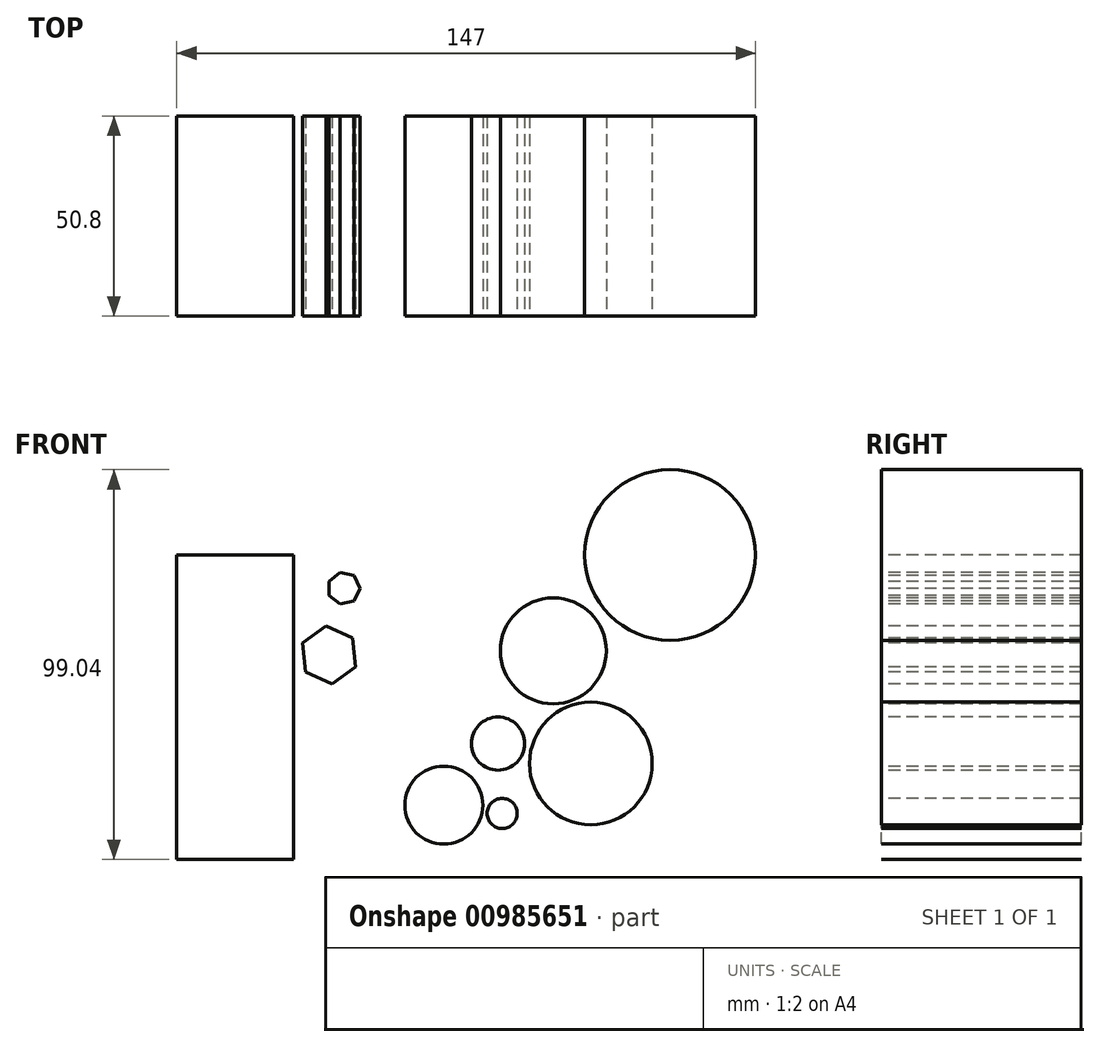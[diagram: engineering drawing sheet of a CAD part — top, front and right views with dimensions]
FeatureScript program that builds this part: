
annotation { "Feature Type Name" : "Feature", "Feature Type Description" : "" }
export const myFeature = defineFeature(function(context is Context, id is Id, definition is map)
    precondition{}
    {
        {
            var Q0;
            Q0=qCreatedBy(makeId("Front.planeOp"),FACE);
            var sketch = newSketch(context, id + "F0", { "sketchPlane" : qUnion([Q0])});
            skLineSegment(sketch, "E0.bottom", {"start": v(-60.54, 36.7) * mm, "end": v(64.78, 36.7) * mm});
            skLineSegment(sketch, "E0.top", {"start": v(-60.54, -40.67) * mm, "end": v(64.78, -40.67) * mm});
            skLineSegment(sketch, "E0.left", {"start": v(-60.54, 36.7) * mm, "end": v(-60.54, -40.67) * mm});
            skLineSegment(sketch, "E0.right", {"start": v(64.78, 36.7) * mm, "end": v(64.78, -40.67) * mm});
            skLineSegment(sketch, "E1.bottom", {"start": v(-60.54, 36.7) * mm, "end": v(-30.86, 36.7) * mm});
            skLineSegment(sketch, "E1.top", {"start": v(-60.54, 8.88) * mm, "end": v(-30.86, 8.88) * mm});
            skLineSegment(sketch, "E1.left", {"start": v(-60.54, 36.7) * mm, "end": v(-60.54, 8.88) * mm});
            skLineSegment(sketch, "E1.right", {"start": v(-30.86, 36.7) * mm, "end": v(-30.86, 8.88) * mm});
            skLineSegment(sketch, "E2.bottom", {"start": v(-45.7, 8.88) * mm, "end": v(-30.86, 8.88) * mm});
            skLineSegment(sketch, "E2.top", {"start": v(-45.7, 0) * mm, "end": v(-30.86, 0) * mm});
            skLineSegment(sketch, "E2.left", {"start": v(-45.7, 8.88) * mm, "end": v(-45.7, 0) * mm});
            skLineSegment(sketch, "E2.right", {"start": v(-30.86, 8.88) * mm, "end": v(-30.86, 0) * mm});
            skLineSegment(sketch, "E3.bottom", {"start": v(-38.28, 0) * mm, "end": v(-30.86, 0) * mm});
            skLineSegment(sketch, "E3.top", {"start": v(-38.28, -7.29) * mm, "end": v(-30.86, -7.29) * mm});
            skLineSegment(sketch, "E3.left", {"start": v(-38.28, 0) * mm, "end": v(-38.28, -7.29) * mm});
            skLineSegment(sketch, "E3.right", {"start": v(-30.86, 0) * mm, "end": v(-30.86, -7.29) * mm});
            skLineSegment(sketch, "E4.bottom", {"start": v(-34.57, -7.29) * mm, "end": v(-30.86, -7.29) * mm});
            skLineSegment(sketch, "E4.top", {"start": v(-34.57, -40.67) * mm, "end": v(-30.86, -40.67) * mm});
            skLineSegment(sketch, "E4.left", {"start": v(-34.57, -7.29) * mm, "end": v(-34.57, -40.67) * mm});
            skLineSegment(sketch, "E4.right", {"start": v(-30.86, -7.29) * mm, "end": v(-30.86, -40.67) * mm});
            skCircle(sketch, "E5", {"center": v(64.78, 36.7) * mm, "radius": 21.68 * mm});
            skCircle(sketch, "E6", {"center": v(35.1, 12.32) * mm, "radius": 13.46 * mm});
            skCircle(sketch, "E7", {"center": v(44.64, -16.3) * mm, "radius": 15.59 * mm});
            skCircle(sketch, "E8", {"center": v(7.29, -26.9) * mm, "radius": 9.9 * mm});
            skCircle(sketch, "E9", {"center": v(22.12, -29.01) * mm, "radius": 3.82 * mm});
            skCircle(sketch, "E10", {"center": v(21.06, -11.26) * mm, "radius": 6.75 * mm});
            skCircle(sketch, "E11.cCircle", {"center": v(-18.15, 28.22) * mm, "radius": 3.7 * mm, "construction": true});
            skLineSegment(sketch, "E11.0", {"start": v(-21.86, 26.43) * mm, "end": v(-21.86, 30) * mm});
            skLineSegment(sketch, "E11.1", {"start": v(-21.86, 30) * mm, "end": v(-19.06, 32.23) * mm});
            skLineSegment(sketch, "E11.2", {"start": v(-19.06, 32.23) * mm, "end": v(-15.58, 31.43) * mm});
            skLineSegment(sketch, "E11.3", {"start": v(-15.58, 31.43) * mm, "end": v(-14.03, 28.22) * mm});
            skLineSegment(sketch, "E11.4", {"start": v(-14.03, 28.22) * mm, "end": v(-15.58, 25) * mm});
            skLineSegment(sketch, "E11.5", {"start": v(-15.58, 25) * mm, "end": v(-19.06, 24.2) * mm});
            skLineSegment(sketch, "E11.6", {"start": v(-19.06, 24.2) * mm, "end": v(-21.86, 26.43) * mm});
            skPoint(sketch, "E11.0.midPoint", {"position": v(-21.86, 28.22) * mm});
            skCircle(sketch, "E12.cCircle", {"center": v(-21.86, 11.26) * mm, "radius": 6.4 * mm, "construction": true});
            skLineSegment(sketch, "E12.0", {"start": v(-21.14, 3.9) * mm, "end": v(-27.87, 6.96) * mm});
            skLineSegment(sketch, "E12.1", {"start": v(-27.87, 6.96) * mm, "end": v(-28.59, 14.32) * mm});
            skLineSegment(sketch, "E12.2", {"start": v(-28.59, 14.32) * mm, "end": v(-22.57, 18.62) * mm});
            skLineSegment(sketch, "E12.3", {"start": v(-22.57, 18.62) * mm, "end": v(-15.84, 15.56) * mm});
            skLineSegment(sketch, "E12.4", {"start": v(-15.84, 15.56) * mm, "end": v(-15.13, 8.2) * mm});
            skLineSegment(sketch, "E12.5", {"start": v(-15.13, 8.2) * mm, "end": v(-21.14, 3.9) * mm});
            skPoint(sketch, "E12.0.midPoint", {"position": v(-24.5, 5.43) * mm});
            skSolve(sketch);
        }
        {
            var Q0;
            {var subQ6=sQuery(id+"F0.wireOp",EDGE,"E1.right");Q0=makeQuery(id+"F0.imprint","IMPRINT",FACE,{"disambiguationData":[TD([[makeQuery(id+"F0.imprint","IMPRINT",EDGE,{"derivedFrom":subQ6}),-1.0]])]});}
            var Q1;
            Q1=makeQuery(id+"F0.imprint","IMPRINT",FACE,{"disambiguationData":[TD([[makeQuery(id+"F0.imprint","IMPRINT",EDGE,{"derivedFrom":sQuery(id+"F0.wireOp",EDGE,"E8")}),1.0]])]});
            var Q2;
            Q2=makeQuery(id+"F0.imprint","IMPRINT",FACE,{"disambiguationData":[TD([[makeQuery(id+"F0.imprint","IMPRINT",EDGE,{"derivedFrom":sQuery(id+"F0.wireOp",EDGE,"E12.0")}),-1.0]])]});
            var Q3;
            Q3=makeQuery(id+"F0.imprint","IMPRINT",FACE,{"disambiguationData":[TD([[makeQuery(id+"F0.imprint","IMPRINT",EDGE,{"derivedFrom":sQuery(id+"F0.wireOp",EDGE,"E11.0")}),-1.0]])]});
            var Q4;
            Q4=makeQuery(id+"F0.imprint","IMPRINT",FACE,{"disambiguationData":[TD([[makeQuery(id+"F0.imprint","IMPRINT",EDGE,{"derivedFrom":sQuery(id+"F0.wireOp",EDGE,"E6")}),1.0]])]});
            var Q5;
            {var subQ0=sQuery(id+"F0.wireOp",EDGE,"E0.right");var subQ1=sQuery(id+"F0.wireOp",EDGE,"E0.bottom");var subQ2=makeQuery(id+"F0.imprint","INTERSECT",VERTEX,{"derivedFrom":[subQ1,subQ0]});Q5=makeQuery(id+"F0.imprint","IMPRINT",FACE,{"disambiguationData":[TD([[makeQuery(id+"F0.imprint","IMPRINT",EDGE,{"disambiguationData":[TD([[subQ2,1.0]])],"derivedFrom":subQ1}),-1.0]])]});}
            var Q6;
            {var subQ0=sQuery(id+"F0.wireOp",EDGE,"E0.right");var subQ1=sQuery(id+"F0.wireOp",EDGE,"E0.bottom");var subQ2=makeQuery(id+"F0.imprint","INTERSECT",VERTEX,{"derivedFrom":[subQ1,subQ0]});Q6=makeQuery(id+"F0.imprint","IMPRINT",FACE,{"disambiguationData":[TD([[makeQuery(id+"F0.imprint","IMPRINT",EDGE,{"disambiguationData":[TD([[subQ2,1.0]])],"derivedFrom":subQ1}),1.0]])]});}
            var Q7;
            Q7=makeQuery(id+"F0.imprint","IMPRINT",FACE,{"disambiguationData":[TD([[makeQuery(id+"F0.imprint","IMPRINT",EDGE,{"derivedFrom":sQuery(id+"F0.wireOp",EDGE,"E7")}),1.0]])]});
            var Q8;
            Q8=makeQuery(id+"F0.imprint","IMPRINT",FACE,{"disambiguationData":[TD([[makeQuery(id+"F0.imprint","IMPRINT",EDGE,{"derivedFrom":sQuery(id+"F0.wireOp",EDGE,"E10")}),1.0]])]});
            var Q9;
            Q9=makeQuery(id+"F0.imprint","IMPRINT",FACE,{"disambiguationData":[TD([[makeQuery(id+"F0.imprint","IMPRINT",EDGE,{"derivedFrom":sQuery(id+"F0.wireOp",EDGE,"E9")}),1.0]])]});
            var Q10;
            {var subQ2=sQuery(id+"F0.wireOp",EDGE,"E4.left");Q10=makeQuery(id+"F0.imprint","IMPRINT",FACE,{"disambiguationData":[TD([[makeQuery(id+"F0.imprint","IMPRINT",EDGE,{"derivedFrom":subQ2}),1.0]])]});}
            var Q11;
            {var subQ3=sQuery(id+"F0.wireOp",EDGE,"E3.left");Q11=makeQuery(id+"F0.imprint","IMPRINT",FACE,{"disambiguationData":[TD([[makeQuery(id+"F0.imprint","IMPRINT",EDGE,{"derivedFrom":subQ3}),1.0]])]});}
            var Q12;
            {var subQ0=sQuery(id+"F0.wireOp",EDGE,"E2.left");Q12=makeQuery(id+"F0.imprint","IMPRINT",FACE,{"disambiguationData":[TD([[makeQuery(id+"F0.imprint","IMPRINT",EDGE,{"derivedFrom":subQ0}),-1.0]])]});}
            var Q13;
            {var subQ0=sQuery(id+"F0.wireOp",EDGE,"E2.left");Q13=makeQuery(id+"F0.imprint","IMPRINT",FACE,{"disambiguationData":[TD([[makeQuery(id+"F0.imprint","IMPRINT",EDGE,{"derivedFrom":subQ0}),1.0]])]});}
            extrude(context, id + "F1", {"entities" : qUnion([Q0, Q1, Q2, Q3, Q4, Q5, Q6, Q7, Q8, Q9, Q10, Q11, Q12, Q13]), "oppositeDirection" : true, "depth" : 50.8 * mm, "offsetDistance" : 25.4 * mm});
        }
    });
